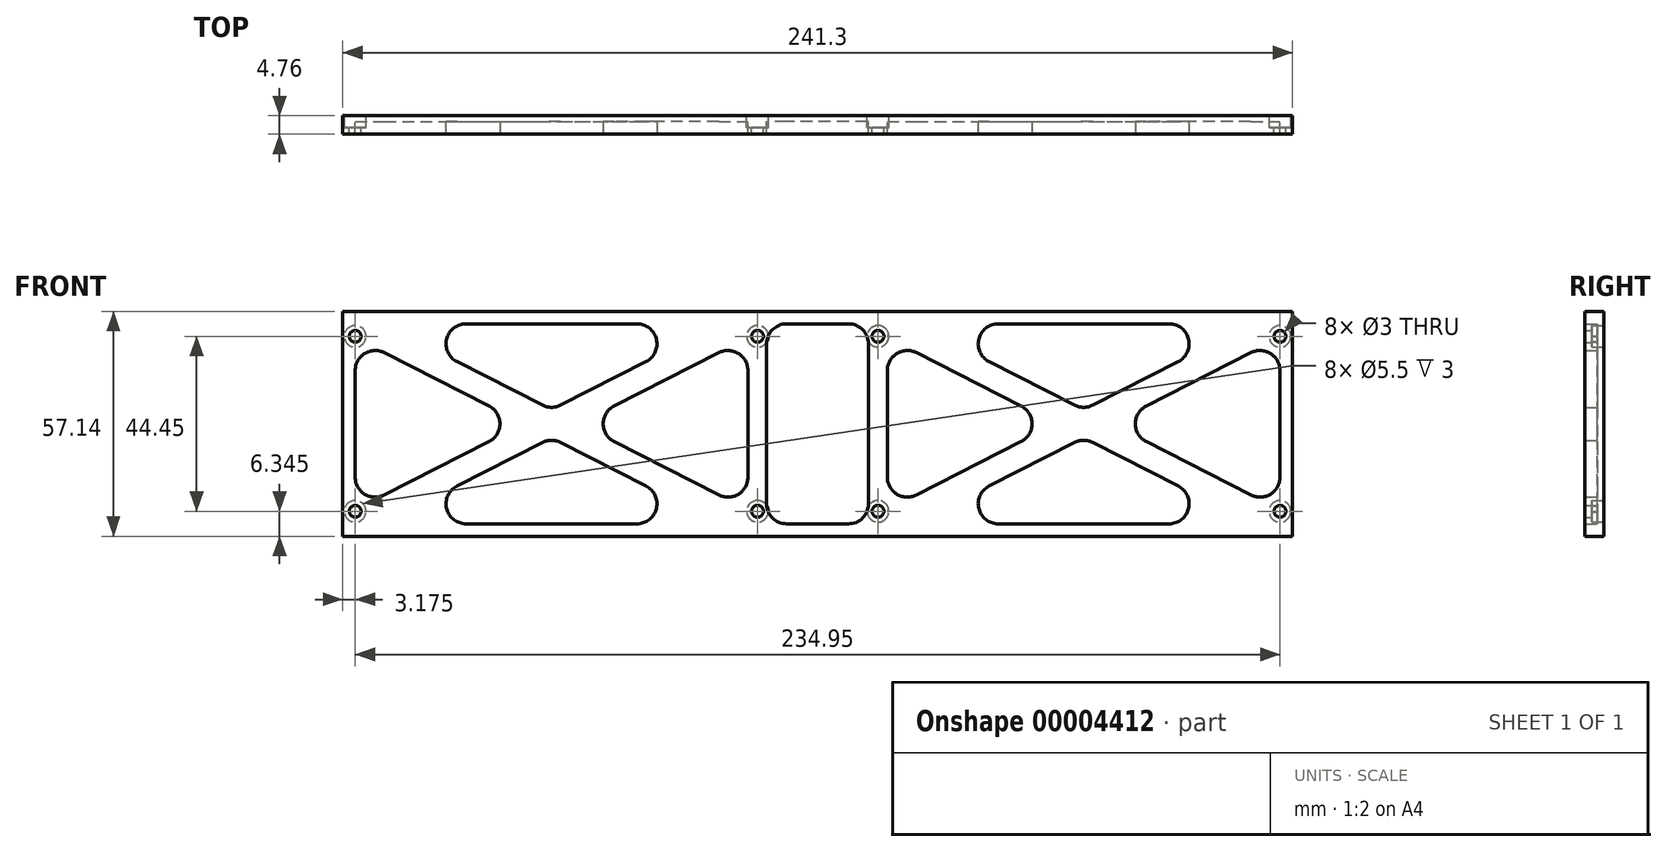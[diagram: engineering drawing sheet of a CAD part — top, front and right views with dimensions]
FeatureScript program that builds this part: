
annotation { "Feature Type Name" : "Feature", "Feature Type Description" : "" }
export const myFeature = defineFeature(function(context is Context, id is Id, definition is map)
    precondition{}
    {
        {
            var Q0;
            Q0=qCreatedBy(makeId("Front.planeOp"),FACE);
            var sketch = newSketch(context, id + "F0", { "sketchPlane" : qUnion([Q0])});
            skLineSegment(sketch, "E0.rect.bottom", {"start": v(120.65, 28.58) * mm, "end": v(-120.65, 28.58) * mm});
            skLineSegment(sketch, "E0.rect.top", {"start": v(120.65, -28.57) * mm, "end": v(-120.65, -28.57) * mm});
            skLineSegment(sketch, "E0.rect.left", {"start": v(120.65, 28.58) * mm, "end": v(120.65, -28.57) * mm});
            skLineSegment(sketch, "E0.rect.right", {"start": v(-120.65, 28.58) * mm, "end": v(-120.65, -28.58) * mm});
            skPoint(sketch, "E0.rect.middle", {"position": v(0, 0) * mm});
            skSolve(sketch);
        }
        {
            var Q0;
            Q0=makeQuery(id+"F0.imprint","IMPRINT",FACE,{"disambiguationData":[TD([[makeQuery(id+"F0.imprint","IMPRINT",EDGE,{"derivedFrom":sQuery(id+"F0.wireOp",EDGE,"E0.rect.bottom")}),1.0]])]});
            extrude(context, id + "F1", {"entities" : qUnion([Q0]), "depth" : 1.59 * mm});
        }
        {
            var Q0;
            Q0=makeQuery(id+"F1.opExtrude","CAP_FACE",FACE,{"disambiguationData":[OSD([sQuery(id+"F0.wireOp",EDGE,"E0.rect.bottom"),sQuery(id+"F0.wireOp",EDGE,"E0.rect.top"),sQuery(id+"F0.wireOp",EDGE,"E0.rect.left"),sQuery(id+"F0.wireOp",EDGE,"E0.rect.right")])],"isStart":false});
            var sketch = newSketch(context, id + "F2", { "sketchPlane" : qUnion([Q0])});
            skLineSegment(sketch, "E1.left", {"start": v(-120.65, 28.58) * mm, "end": v(-120.65, -28.58) * mm});
            skLineSegment(sketch, "E1.right", {"start": v(-117.48, 21.84) * mm, "end": v(-117.48, -21.84) * mm});
            skLineSegment(sketch, "E2.left", {"start": v(120.65, 28.58) * mm, "end": v(120.65, -28.57) * mm});
            skLineSegment(sketch, "E2.right", {"start": v(117.48, 21.84) * mm, "end": v(117.48, -21.84) * mm});
            skLineSegment(sketch, "E3.top", {"start": v(-110.48, 25.4) * mm, "end": v(-24.71, 25.4) * mm});
            skLineSegment(sketch, "E4.top", {"start": v(110.48, -25.4) * mm, "end": v(24.71, -25.4) * mm});
            skLineSegment(sketch, "E5.trimOffspring", {"start": v(-12.95, 25.4) * mm, "end": v(12.95, 25.4) * mm});
            skLineSegment(sketch, "E6.trimOffspring", {"start": v(24.71, 25.4) * mm, "end": v(110.48, 25.4) * mm});
            skLineSegment(sketch, "E7.trimOffspring", {"start": v(-24.71, -25.4) * mm, "end": v(-110.48, -25.4) * mm});
            skLineSegment(sketch, "E8.trimOffspring", {"start": v(12.95, -25.4) * mm, "end": v(-12.95, -25.4) * mm});
            skLineSegment(sketch, "E9", {"start": v(-120.65, 28.58) * mm, "end": v(120.65, 28.58) * mm});
            skLineSegment(sketch, "E10", {"start": v(120.65, -28.58) * mm, "end": v(-120.65, -28.58) * mm});
            skLineSegment(sketch, "E11", {"start": v(-120.65, 28.57) * mm, "end": v(-117.48, 25.4) * mm, "construction": true});
            skLineSegment(sketch, "E12", {"start": v(-117.48, -25.4) * mm, "end": v(-120.65, -28.58) * mm, "construction": true});
            skLineSegment(sketch, "E13", {"start": v(-117.48, 25.4) * mm, "end": v(-17.72, -25.4) * mm, "construction": true});
            skLineSegment(sketch, "E14", {"start": v(-17.72, 25.4) * mm, "end": v(-117.48, -25.4) * mm, "construction": true});
            skLineSegment(sketch, "E15", {"start": v(17.72, 25.4) * mm, "end": v(117.48, -25.4) * mm, "construction": true});
            skLineSegment(sketch, "E16", {"start": v(117.48, 25.4) * mm, "end": v(17.72, -25.4) * mm, "construction": true});
            skLineSegment(sketch, "E17", {"start": v(12.95, -25.4) * mm, "end": v(12.95, 25.4) * mm});
            skLineSegment(sketch, "E18", {"start": v(17.72, 21.84) * mm, "end": v(17.72, -21.84) * mm});
            skLineSegment(sketch, "E19", {"start": v(-12.95, 25.4) * mm, "end": v(-12.95, -25.4) * mm});
            skLineSegment(sketch, "E20", {"start": v(-17.72, 21.84) * mm, "end": v(-17.72, -21.84) * mm});
            skLineSegment(sketch, "E21.0", {"start": v(-24.71, 25.4) * mm, "end": v(-67.6, 3.56) * mm});
            skLineSegment(sketch, "E22.0", {"start": v(-17.72, 21.84) * mm, "end": v(-60.6, 0) * mm});
            skLineSegment(sketch, "E23.0", {"start": v(-117.48, 21.84) * mm, "end": v(-74.6, 0) * mm});
            skLineSegment(sketch, "E24.0", {"start": v(-110.48, 25.4) * mm, "end": v(-67.6, 3.56) * mm});
            skLineSegment(sketch, "E25.0", {"start": v(17.72, 21.84) * mm, "end": v(60.6, 0) * mm});
            skLineSegment(sketch, "E26.0", {"start": v(24.71, 25.4) * mm, "end": v(67.6, 3.56) * mm});
            skLineSegment(sketch, "E27.0", {"start": v(110.48, 25.4) * mm, "end": v(67.6, 3.56) * mm});
            skLineSegment(sketch, "E28.0", {"start": v(117.48, 21.84) * mm, "end": v(74.6, 0) * mm});
            skLineSegment(sketch, "E29.trimOffspring", {"start": v(-71.1, -1.78) * mm, "end": v(-24.71, -25.4) * mm});
            skLineSegment(sketch, "E30.trimOffspring", {"start": v(-74.6, 0) * mm, "end": v(-117.48, -21.84) * mm});
            skLineSegment(sketch, "E31.trimOffspring", {"start": v(-60.6, 0) * mm, "end": v(-17.72, -21.84) * mm});
            skLineSegment(sketch, "E32.trimOffspring", {"start": v(-67.6, -3.56) * mm, "end": v(-110.48, -25.4) * mm});
            skLineSegment(sketch, "E33.trimOffspring", {"start": v(67.6, -3.56) * mm, "end": v(110.48, -25.4) * mm});
            skLineSegment(sketch, "E34.trimOffspring", {"start": v(60.6, 0) * mm, "end": v(17.72, -21.84) * mm});
            skLineSegment(sketch, "E35.trimOffspring", {"start": v(67.6, -3.56) * mm, "end": v(24.71, -25.4) * mm});
            skLineSegment(sketch, "E36.trimOffspring", {"start": v(74.6, 0) * mm, "end": v(117.48, -21.84) * mm});
            skSolve(sketch);
        }
        {
            var Q0;
            Q0=makeQuery(id+"F2.imprint","IMPRINT",FACE,{"disambiguationData":[TD([[makeQuery(id+"F2.imprint","IMPRINT",EDGE,{"derivedFrom":sQuery(id+"F2.wireOp",EDGE,"E1.left")}),1.0]])]});
            extrude(context, id + "F3", {"entities" : qUnion([Q0]), "operationType" : NewBodyOperationType.ADD, "depth" : 3.17 * mm});
        }
        {
            var Q0;
            Q0=makeQuery(id+"F3.opExtrude","SWEPT_EDGE",EDGE,{"disambiguationData":[OSD([sQuery(id+"F2.wireOp",EDGE,"E20"),sQuery(id+"F2.wireOp",EDGE,"E22.0")])]});
            var Q1;
            Q1=makeQuery(id+"F3.opExtrude","SWEPT_EDGE",EDGE,{"disambiguationData":[OSD([sQuery(id+"F2.wireOp",EDGE,"E5.trimOffspring"),sQuery(id+"F2.wireOp",EDGE,"E17")])]});
            var Q2;
            Q2=makeQuery(id+"F3.opExtrude","SWEPT_EDGE",EDGE,{"disambiguationData":[OSD([sQuery(id+"F2.wireOp",EDGE,"E29.trimOffspring"),sQuery(id+"F2.wireOp",EDGE,"E32.trimOffspring")])]});
            var Q3;
            Q3=makeQuery(id+"F3.opExtrude","SWEPT_EDGE",EDGE,{"disambiguationData":[OSD([sQuery(id+"F2.wireOp",EDGE,"E3.top"),sQuery(id+"F2.wireOp",EDGE,"E24.0")])]});
            var Q4;
            Q4=makeQuery(id+"F3.opExtrude","SWEPT_EDGE",EDGE,{"disambiguationData":[OSD([sQuery(id+"F2.wireOp",EDGE,"E1.right"),sQuery(id+"F2.wireOp",EDGE,"E23.0")])]});
            var Q5;
            Q5=makeQuery(id+"F3.opExtrude","SWEPT_EDGE",EDGE,{"disambiguationData":[OSD([sQuery(id+"F2.wireOp",EDGE,"E5.trimOffspring"),sQuery(id+"F2.wireOp",EDGE,"E19")])]});
            var Q6;
            Q6=makeQuery(id+"F3.opExtrude","SWEPT_EDGE",EDGE,{"disambiguationData":[OSD([sQuery(id+"F2.wireOp",EDGE,"E18"),sQuery(id+"F2.wireOp",EDGE,"E25.0")])]});
            var Q7;
            Q7=makeQuery(id+"F3.opExtrude","SWEPT_EDGE",EDGE,{"disambiguationData":[OSD([sQuery(id+"F2.wireOp",EDGE,"E33.trimOffspring"),sQuery(id+"F2.wireOp",EDGE,"E35.trimOffspring")])]});
            var Q8;
            Q8=makeQuery(id+"F3.opExtrude","SWEPT_EDGE",EDGE,{"disambiguationData":[OSD([sQuery(id+"F2.wireOp",EDGE,"E8.trimOffspring"),sQuery(id+"F2.wireOp",EDGE,"E17")])]});
            var Q9;
            Q9=makeQuery(id+"F3.opExtrude","SWEPT_EDGE",EDGE,{"disambiguationData":[OSD([sQuery(id+"F2.wireOp",EDGE,"E2.right"),sQuery(id+"F2.wireOp",EDGE,"E36.trimOffspring")])]});
            var Q10;
            Q10=makeQuery(id+"F3.opExtrude","SWEPT_EDGE",EDGE,{"disambiguationData":[OSD([sQuery(id+"F2.wireOp",EDGE,"E26.0"),sQuery(id+"F2.wireOp",EDGE,"E27.0")])]});
            var Q11;
            Q11=makeQuery(id+"F3.opExtrude","SWEPT_EDGE",EDGE,{"disambiguationData":[OSD([sQuery(id+"F2.wireOp",EDGE,"E21.0"),sQuery(id+"F2.wireOp",EDGE,"E24.0")])]});
            var Q12;
            Q12=makeQuery(id+"F3.opExtrude","SWEPT_EDGE",EDGE,{"disambiguationData":[OSD([sQuery(id+"F2.wireOp",EDGE,"E20"),sQuery(id+"F2.wireOp",EDGE,"E31.trimOffspring")])]});
            var Q13;
            Q13=makeQuery(id+"F3.opExtrude","SWEPT_EDGE",EDGE,{"disambiguationData":[OSD([sQuery(id+"F2.wireOp",EDGE,"E3.top"),sQuery(id+"F2.wireOp",EDGE,"E21.0")])]});
            var Q14;
            Q14=makeQuery(id+"F3.opExtrude","SWEPT_EDGE",EDGE,{"disambiguationData":[OSD([sQuery(id+"F2.wireOp",EDGE,"E23.0"),sQuery(id+"F2.wireOp",EDGE,"E30.trimOffspring")])]});
            var Q15;
            Q15=makeQuery(id+"F3.opExtrude","SWEPT_EDGE",EDGE,{"disambiguationData":[OSD([sQuery(id+"F2.wireOp",EDGE,"E6.trimOffspring"),sQuery(id+"F2.wireOp",EDGE,"E27.0")])]});
            var Q16;
            Q16=makeQuery(id+"F3.opExtrude","SWEPT_EDGE",EDGE,{"disambiguationData":[OSD([sQuery(id+"F2.wireOp",EDGE,"E25.0"),sQuery(id+"F2.wireOp",EDGE,"E34.trimOffspring")])]});
            var Q17;
            Q17=makeQuery(id+"F3.opExtrude","SWEPT_EDGE",EDGE,{"disambiguationData":[OSD([sQuery(id+"F2.wireOp",EDGE,"E7.trimOffspring"),sQuery(id+"F2.wireOp",EDGE,"E29.trimOffspring")])]});
            var Q18;
            Q18=makeQuery(id+"F3.opExtrude","SWEPT_EDGE",EDGE,{"disambiguationData":[OSD([sQuery(id+"F2.wireOp",EDGE,"E4.top"),sQuery(id+"F2.wireOp",EDGE,"E33.trimOffspring")])]});
            var Q19;
            Q19=makeQuery(id+"F3.opExtrude","SWEPT_EDGE",EDGE,{"disambiguationData":[OSD([sQuery(id+"F2.wireOp",EDGE,"E2.right"),sQuery(id+"F2.wireOp",EDGE,"E28.0")])]});
            var Q20;
            Q20=makeQuery(id+"F3.opExtrude","SWEPT_EDGE",EDGE,{"disambiguationData":[OSD([sQuery(id+"F2.wireOp",EDGE,"E28.0"),sQuery(id+"F2.wireOp",EDGE,"E36.trimOffspring")])]});
            var Q21;
            Q21=makeQuery(id+"F3.opExtrude","SWEPT_EDGE",EDGE,{"disambiguationData":[OSD([sQuery(id+"F2.wireOp",EDGE,"E22.0"),sQuery(id+"F2.wireOp",EDGE,"E31.trimOffspring")])]});
            var Q22;
            Q22=makeQuery(id+"F3.opExtrude","SWEPT_EDGE",EDGE,{"disambiguationData":[OSD([sQuery(id+"F2.wireOp",EDGE,"E18"),sQuery(id+"F2.wireOp",EDGE,"E34.trimOffspring")])]});
            var Q23;
            Q23=makeQuery(id+"F3.opExtrude","SWEPT_EDGE",EDGE,{"disambiguationData":[OSD([sQuery(id+"F2.wireOp",EDGE,"E4.top"),sQuery(id+"F2.wireOp",EDGE,"E35.trimOffspring")])]});
            var Q24;
            Q24=makeQuery(id+"F3.opExtrude","SWEPT_EDGE",EDGE,{"disambiguationData":[OSD([sQuery(id+"F2.wireOp",EDGE,"E7.trimOffspring"),sQuery(id+"F2.wireOp",EDGE,"E32.trimOffspring")])]});
            var Q25;
            Q25=makeQuery(id+"F3.opExtrude","SWEPT_EDGE",EDGE,{"disambiguationData":[OSD([sQuery(id+"F2.wireOp",EDGE,"E8.trimOffspring"),sQuery(id+"F2.wireOp",EDGE,"E19")])]});
            var Q26;
            Q26=makeQuery(id+"F3.opExtrude","SWEPT_EDGE",EDGE,{"disambiguationData":[OSD([sQuery(id+"F2.wireOp",EDGE,"E1.right"),sQuery(id+"F2.wireOp",EDGE,"E30.trimOffspring")])]});
            var Q27;
            Q27=makeQuery(id+"F3.opExtrude","SWEPT_EDGE",EDGE,{"disambiguationData":[OSD([sQuery(id+"F2.wireOp",EDGE,"E6.trimOffspring"),sQuery(id+"F2.wireOp",EDGE,"E26.0")])]});
            fillet(context, id + "F4", {"entities" : qUnion([Q0, Q1, Q2, Q3, Q4, Q5, Q6, Q7, Q8, Q9, Q10, Q11, Q12, Q13, Q14, Q15, Q16, Q17, Q18, Q19, Q20, Q21, Q22, Q23, Q24, Q25, Q26, Q27]), "radius" : 5.08 * mm, "tangentPropagation" : true, "allowEdgeOverflow" : false});
        }
        {
            var Q0;
            Q0=makeQuery(id+"F1.opExtrude","CAP_FACE",FACE,{"disambiguationData":[OSD([sQuery(id+"F0.wireOp",EDGE,"E0.rect.bottom"),sQuery(id+"F0.wireOp",EDGE,"E0.rect.top"),sQuery(id+"F0.wireOp",EDGE,"E0.rect.left"),sQuery(id+"F0.wireOp",EDGE,"E0.rect.right")])],"isStart":true});
            var sketch = newSketch(context, id + "F5", { "sketchPlane" : qUnion([Q0])});
            skCircle(sketch, "E37", {"center": v(-117.48, 22.23) * mm, "radius": 1.5 * mm});
            skCircle(sketch, "E38", {"center": v(-117.48, -22.22) * mm, "radius": 1.5 * mm});
            skCircle(sketch, "E39", {"center": v(-15.34, -22.22) * mm, "radius": 1.5 * mm});
            skCircle(sketch, "E40", {"center": v(-15.34, 22.23) * mm, "radius": 1.5 * mm});
            skCircle(sketch, "E41", {"center": v(15.27, 22.23) * mm, "radius": 1.5 * mm});
            skCircle(sketch, "E42", {"center": v(15.27, -22.22) * mm, "radius": 1.5 * mm});
            skCircle(sketch, "E43", {"center": v(117.48, -22.22) * mm, "radius": 1.5 * mm});
            skCircle(sketch, "E44", {"center": v(117.48, 22.23) * mm, "radius": 1.5 * mm});
            skSolve(sketch);
        }
        {
            var Q0;
            Q0 = qSketchRegion(id + "F5", true);
            extrude(context, id + "F6", {"entities" : qUnion([Q0]), "operationType" : NewBodyOperationType.REMOVE, "endBound" : BoundingType.THROUGH_ALL, "oppositeDirection" : true, "depth" : 25.4 * mm});
        }
        {
            var Q0;
            Q0=makeQuery(id+"F1.opExtrude","CAP_FACE",FACE,{"disambiguationData":[OSD([sQuery(id+"F0.wireOp",EDGE,"E0.rect.bottom"),sQuery(id+"F0.wireOp",EDGE,"E0.rect.top"),sQuery(id+"F0.wireOp",EDGE,"E0.rect.left"),sQuery(id+"F0.wireOp",EDGE,"E0.rect.right")])],"isStart":true});
            var sketch = newSketch(context, id + "F7", { "sketchPlane" : qUnion([Q0])});
            skCircle(sketch, "E45", {"center": v(-117.48, 22.23) * mm, "radius": 2.75 * mm});
            skCircle(sketch, "E46", {"center": v(-117.48, -22.22) * mm, "radius": 2.75 * mm});
            skCircle(sketch, "E47", {"center": v(-15.34, 22.23) * mm, "radius": 2.75 * mm});
            skCircle(sketch, "E48", {"center": v(15.27, 22.23) * mm, "radius": 2.75 * mm});
            skCircle(sketch, "E49", {"center": v(-15.34, -22.22) * mm, "radius": 2.75 * mm});
            skCircle(sketch, "E50", {"center": v(15.27, -22.22) * mm, "radius": 2.75 * mm});
            skCircle(sketch, "E51", {"center": v(117.48, 22.23) * mm, "radius": 2.75 * mm});
            skCircle(sketch, "E52", {"center": v(117.48, -22.22) * mm, "radius": 2.75 * mm});
            skSolve(sketch);
        }
        {
            var Q0;
            Q0 = qSketchRegion(id + "F7", true);
            extrude(context, id + "F8", {"entities" : qUnion([Q0]), "operationType" : NewBodyOperationType.REMOVE, "oppositeDirection" : true, "depth" : 3 * mm});
        }
    });
